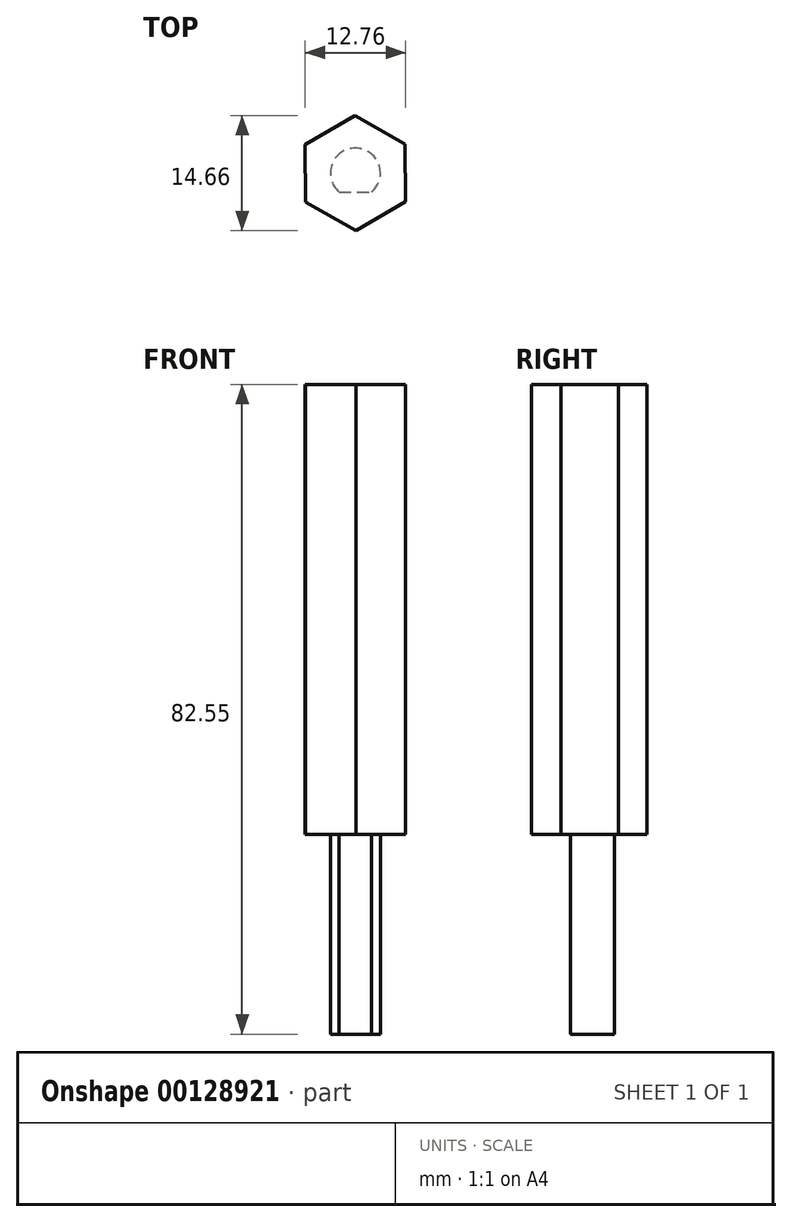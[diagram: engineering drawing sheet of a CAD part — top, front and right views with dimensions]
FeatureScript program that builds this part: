
annotation { "Feature Type Name" : "Feature", "Feature Type Description" : "" }
export const myFeature = defineFeature(function(context is Context, id is Id, definition is map)
    precondition{}
    {
        {
            var Q0;
            Q0=qCreatedBy(makeId("Top.planeOp"),FACE);
            var sketch = newSketch(context, id + "F0", { "sketchPlane" : qUnion([Q0])});
            skCircle(sketch, "E0.cCircle", {"center": v(0, 0) * mm, "radius": 6.35 * mm, "construction": true});
            skLineSegment(sketch, "E0.0", {"start": v(6.38, -3.62) * mm, "end": v(0.05, -7.33) * mm});
            skLineSegment(sketch, "E0.1", {"start": v(0.05, -7.33) * mm, "end": v(-6.32, -3.71) * mm});
            skLineSegment(sketch, "E0.2", {"start": v(-6.32, -3.71) * mm, "end": v(-6.38, 3.62) * mm});
            skLineSegment(sketch, "E0.3", {"start": v(-6.38, 3.62) * mm, "end": v(-0.05, 7.33) * mm});
            skLineSegment(sketch, "E0.4", {"start": v(-0.05, 7.33) * mm, "end": v(6.32, 3.71) * mm});
            skLineSegment(sketch, "E0.5", {"start": v(6.32, 3.71) * mm, "end": v(6.38, -3.62) * mm});
            skPoint(sketch, "E0.0.midPoint", {"position": v(3.21, -5.48) * mm});
            skSolve(sketch);
        }
        {
            var Q0;
            Q0=makeQuery(id+"F0.imprint","IMPRINT",FACE,{"disambiguationData":[TD([[makeQuery(id+"F0.imprint","IMPRINT",EDGE,{"derivedFrom":sQuery(id+"F0.wireOp",EDGE,"E0.0")}),-1.0]])]});
            extrude(context, id + "F1", {"entities" : qUnion([Q0]), "depth" : 57.15 * mm});
        }
        {
            var Q0;
            Q0=qCreatedBy(makeId("Top.planeOp"),FACE);
            var sketch = newSketch(context, id + "F2", { "sketchPlane" : qUnion([Q0])});
            skArc(sketch, "E1", {"start": v(2.07, -2.4) * mm, "mid": v(0, 3.17) * mm, "end": v(-2.07, -2.4) * mm});
            skLineSegment(sketch, "E2", {"start": v(-2.07, -2.4) * mm, "end": v(2.07, -2.4) * mm});
            skSolve(sketch);
        }
        {
            var Q0;
            Q0 = qSketchRegion(id + "F2", true);
            extrude(context, id + "F3", {"entities" : qUnion([Q0]), "operationType" : NewBodyOperationType.ADD, "oppositeDirection" : true, "depth" : 25.4 * mm});
        }
    });
